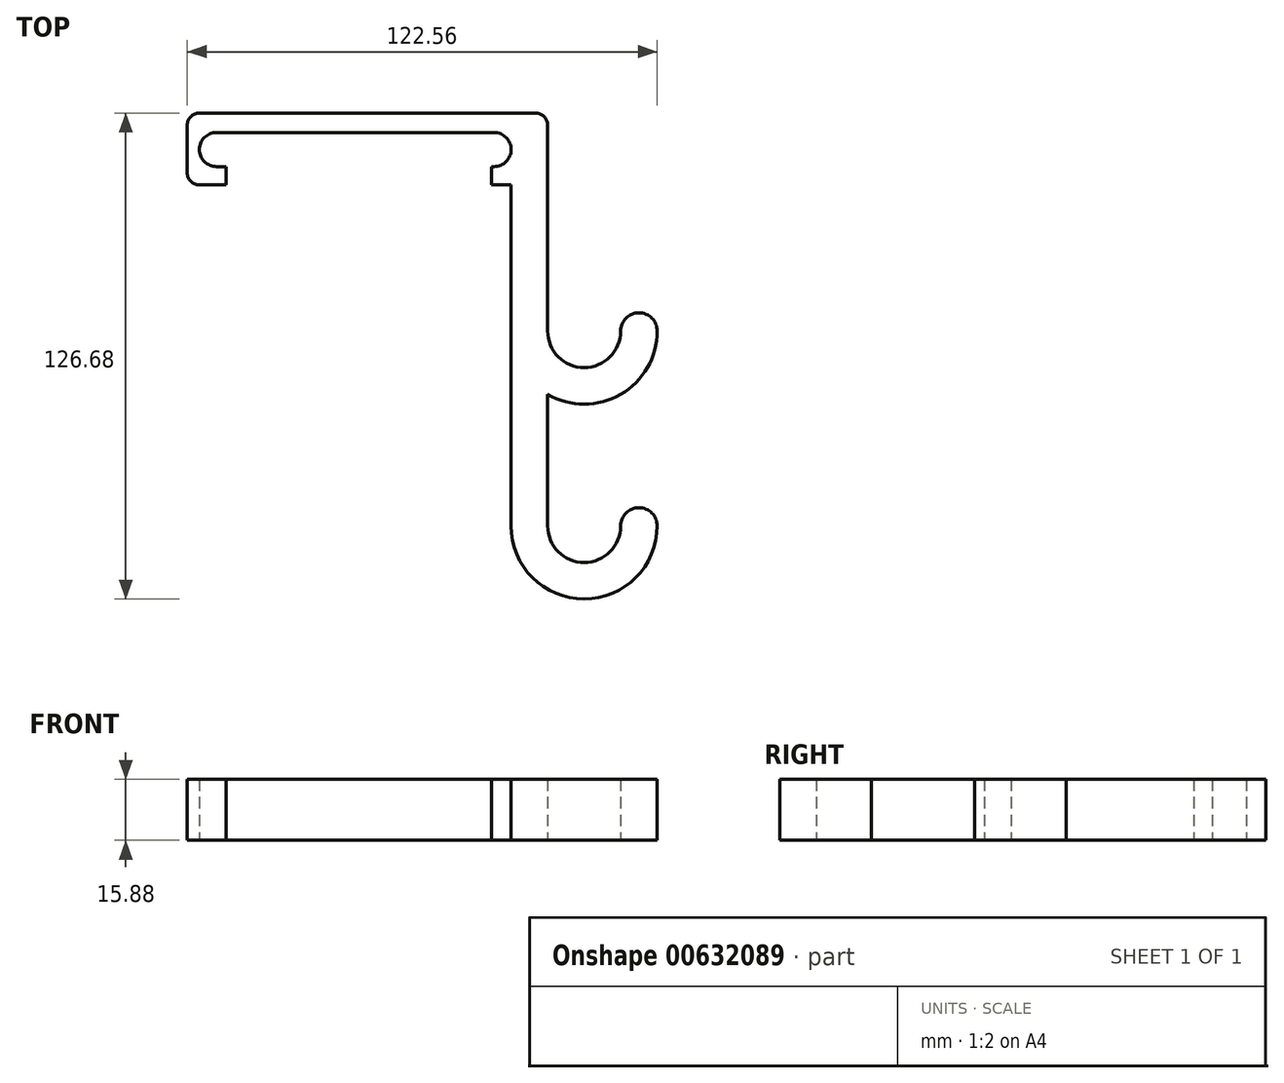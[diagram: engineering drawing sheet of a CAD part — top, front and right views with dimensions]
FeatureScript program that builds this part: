
annotation { "Feature Type Name" : "Feature", "Feature Type Description" : "" }
export const myFeature = defineFeature(function(context is Context, id is Id, definition is map)
    precondition{}
    {
        {
            var Q0;
            Q0=qCreatedBy(makeId("Top.planeOp"),FACE);
            var sketch = newSketch(context, id + "F0", { "sketchPlane" : qUnion([Q0])});
            skLineSegment(sketch, "E0", {"start": v(3.17, 0) * mm, "end": v(90.8, 0) * mm});
            skLineSegment(sketch, "E1", {"start": v(93.98, -3.17) * mm, "end": v(93.98, -56.83) * mm});
            skLineSegment(sketch, "E2", {"start": v(103.5, -66.36) * mm, "end": v(103.5, -66.36) * mm});
            skLineSegment(sketch, "E3", {"start": v(113.03, -56.83) * mm, "end": v(113.03, -56.83) * mm});
            skLineSegment(sketch, "E4", {"start": v(0, -3.18) * mm, "end": v(0, -15.56) * mm});
            skLineSegment(sketch, "E5", {"start": v(3.18, -18.73) * mm, "end": v(10.16, -18.73) * mm});
            skLineSegment(sketch, "E6", {"start": v(10.16, -18.73) * mm, "end": v(10.16, -13.97) * mm});
            skLineSegment(sketch, "E7", {"start": v(10.16, -13.97) * mm, "end": v(7.62, -13.97) * mm});
            skLineSegment(sketch, "E8", {"start": v(3.18, -9.53) * mm, "end": v(3.18, -9.53) * mm});
            skLineSegment(sketch, "E9", {"start": v(84.46, -18.73) * mm, "end": v(84.46, -56.83) * mm});
            skLineSegment(sketch, "E10", {"start": v(103.5, -75.88) * mm, "end": v(103.5, -75.88) * mm});
            skLineSegment(sketch, "E11", {"start": v(122.56, -56.83) * mm, "end": v(122.56, -56.83) * mm});
            skLineSegment(sketch, "E12", {"start": v(7.62, -5.08) * mm, "end": v(80.01, -5.08) * mm});
            skLineSegment(sketch, "E13", {"start": v(84.46, -9.52) * mm, "end": v(84.46, -9.52) * mm});
            skLineSegment(sketch, "E14", {"start": v(79.38, -13.97) * mm, "end": v(79.38, -18.73) * mm});
            skLineSegment(sketch, "E15", {"start": v(79.38, -18.73) * mm, "end": v(84.46, -18.73) * mm});
            skPoint(sketch, "E16.visualSharp", {"position": v(3.17, -5.08) * mm});
            skArc(sketch, "E16.filletArc", {"start": v(7.62, -5.08) * mm, "mid": v(4.48, -6.38) * mm, "end": v(3.18, -9.53) * mm});
            skPoint(sketch, "E17.visualSharp", {"position": v(3.18, -13.97) * mm});
            skArc(sketch, "E17.filletArc", {"start": v(3.17, -9.53) * mm, "mid": v(4.48, -12.67) * mm, "end": v(7.62, -13.97) * mm});
            skPoint(sketch, "E18.visualSharp", {"position": v(84.46, -13.97) * mm});
            skArc(sketch, "E18.filletArc", {"start": v(80.01, -13.97) * mm, "mid": v(83.15, -12.67) * mm, "end": v(84.46, -9.52) * mm});
            skPoint(sketch, "E19.visualSharp", {"position": v(84.46, -5.08) * mm});
            skArc(sketch, "E19.filletArc", {"start": v(84.46, -9.52) * mm, "mid": v(83.15, -6.38) * mm, "end": v(80.01, -5.08) * mm});
            skLineSegment(sketch, "E20", {"start": v(79.38, -13.97) * mm, "end": v(80.01, -13.97) * mm});
            skPoint(sketch, "E21.visualSharp", {"position": v(93.98, -66.36) * mm});
            skArc(sketch, "E21.filletArc", {"start": v(93.98, -56.83) * mm, "mid": v(96.77, -63.57) * mm, "end": v(103.5, -66.36) * mm});
            skPoint(sketch, "E22.visualSharp", {"position": v(113.03, -66.36) * mm});
            skArc(sketch, "E22.filletArc", {"start": v(103.5, -66.36) * mm, "mid": v(110.24, -63.57) * mm, "end": v(113.03, -56.83) * mm});
            skPoint(sketch, "E23.visualSharp", {"position": v(84.46, -75.88) * mm});
            skArc(sketch, "E23.filletArc", {"start": v(93.98, -73.33) * mm, "mid": v(98.57, -75.23) * mm, "end": v(103.5, -75.88) * mm});
            skPoint(sketch, "E24.visualSharp", {"position": v(122.56, -75.88) * mm});
            skArc(sketch, "E24.filletArc", {"start": v(103.5, -75.88) * mm, "mid": v(116.98, -70.3) * mm, "end": v(122.56, -56.83) * mm});
            skArc(sketch, "E25", {"start": v(122.56, -56.83) * mm, "mid": v(117.8, -52.07) * mm, "end": v(113.03, -56.83) * mm});
            skPoint(sketch, "E26.visualSharp", {"position": v(0, 0) * mm});
            skArc(sketch, "E26.filletArc", {"start": v(3.17, 0) * mm, "mid": v(0.93, -0.93) * mm, "end": v(0, -3.18) * mm});
            skPoint(sketch, "E27.visualSharp", {"position": v(0, -18.73) * mm});
            skArc(sketch, "E27.filletArc", {"start": v(0, -15.56) * mm, "mid": v(0.93, -17.8) * mm, "end": v(3.18, -18.73) * mm});
            skPoint(sketch, "E28.visualSharp", {"position": v(93.98, 0) * mm});
            skArc(sketch, "E28.filletArc", {"start": v(93.98, -3.17) * mm, "mid": v(93.05, -0.93) * mm, "end": v(90.8, 0) * mm});
            skArc(sketch, "E29.filletArc", {"start": v(93.98, -107.63) * mm, "mid": v(96.77, -114.37) * mm, "end": v(103.5, -117.16) * mm});
            skArc(sketch, "E30.filletArc", {"start": v(103.5, -117.16) * mm, "mid": v(110.24, -114.37) * mm, "end": v(113.03, -107.63) * mm});
            skArc(sketch, "E31.filletArc", {"start": v(84.46, -107.63) * mm, "mid": v(90.03, -121.1) * mm, "end": v(103.5, -126.68) * mm});
            skArc(sketch, "E32.filletArc", {"start": v(103.5, -126.68) * mm, "mid": v(116.98, -121.1) * mm, "end": v(122.56, -107.63) * mm});
            skArc(sketch, "E33", {"start": v(122.56, -107.63) * mm, "mid": v(117.8, -102.87) * mm, "end": v(113.03, -107.63) * mm});
            skLineSegment(sketch, "E34", {"start": v(84.46, -56.83) * mm, "end": v(84.46, -107.63) * mm});
            skLineSegment(sketch, "E35.trimOffspring", {"start": v(93.98, -73.33) * mm, "end": v(93.98, -107.63) * mm});
            skSolve(sketch);
        }
        {
            var Q0;
            Q0=qSketchRegion(id+"F0",true);
            extrude(context, id + "F1", {"entities" : qUnion([Q0]), "depth" : 15.88 * mm, "offsetDistance" : 25.4 * mm});
        }
    });
